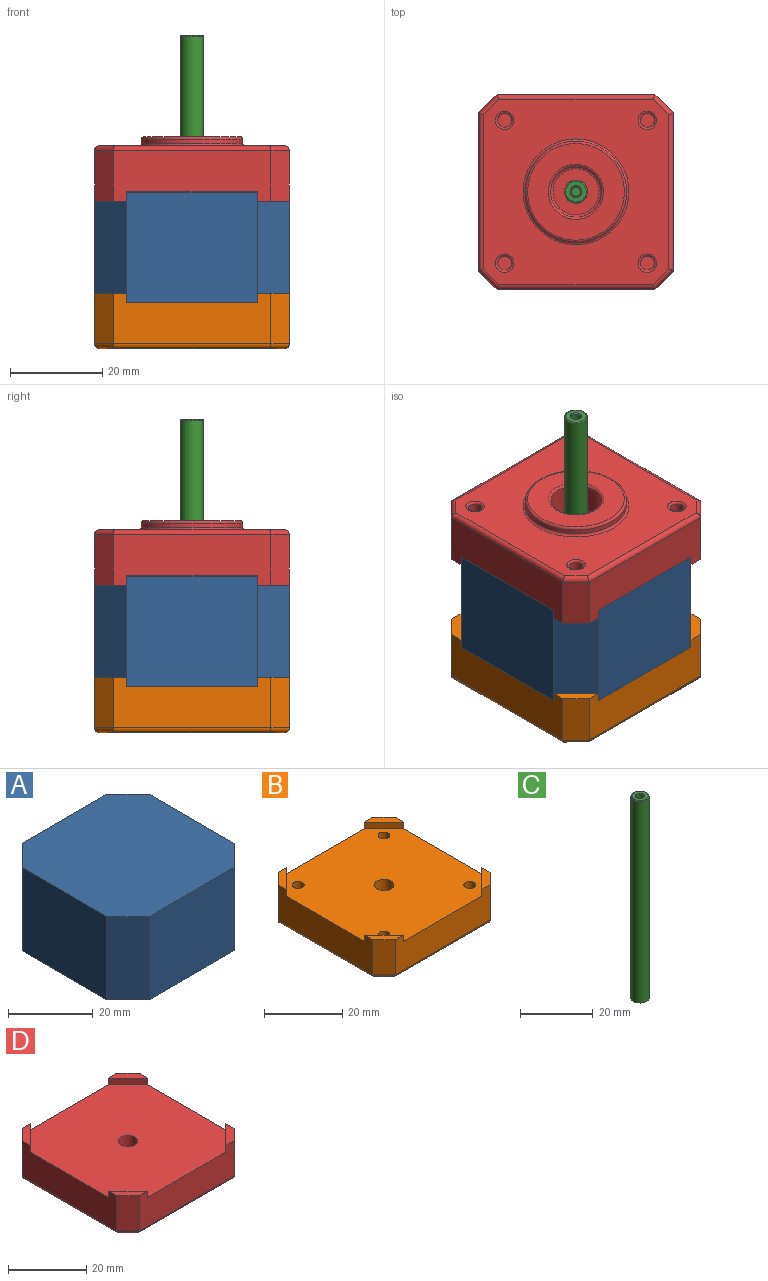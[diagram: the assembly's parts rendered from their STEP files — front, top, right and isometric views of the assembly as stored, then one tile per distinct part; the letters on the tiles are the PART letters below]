
ASSEMBLY  parts=4 mates=3
PART A: 10 faces, bbox 42.3x42.3x24 mm
  f0: plane 28.3x24mm, normal (-1,0,0), area 679.2mm2, adj f1,f7,f8,f9
  f1: plane 24x7mm, normal (-0.71,-0.71,0), area 237.6mm2, adj f0,f2,f8,f9
  f2: plane 28.3x24mm, normal (0,-1,0), area 679.2mm2, adj f1,f3,f8,f9
  f3: plane 24x7mm, normal (0.71,-0.71,0), area 237.6mm2, adj f2,f4,f8,f9
  f4: plane 28.3x24mm, normal (1,0,0), area 679.2mm2, adj f3,f5,f8,f9
  f5: plane 24x7mm, normal (0.71,0.71,0), area 237.6mm2, adj f4,f6,f8,f9
  f6: plane 28.3x24mm, normal (0,1,0), area 679.2mm2, adj f5,f7,f8,f9
  f7: plane 24x7mm, normal (-0.71,0.71,0), area 237.6mm2, adj f0,f6,f8,f9
  f8: plane 42.3x42.3mm, normal (0,0,1), area 1691.3mm2, adj f0,f1,f2,f3,f4,f5,f6,f7
  f9: plane 42.3x42.3mm, normal (0,0,-1), area 1691.3mm2, adj f0,f1,f2,f3,f4,f5,f6,f7
PART B: 50 faces, bbox 42.3x42.3x12 mm
  f0: cylinder r=2.5mm len=5mm, axis (0,0,-1), area 78.5mm2, adj f36,f37
  f1: torus R=3.6mm, axis (0,0,1), area 16.2mm2, adj f11,f31
  f2: torus R=2.6mm, axis (0,0,-1), area 14.4mm2, adj f11,f46
  f3: torus R=3.6mm, axis (0,0,1), area 16.2mm2, adj f10,f31
  f4: torus R=2.6mm, axis (0,0,-1), area 14.4mm2, adj f10,f47
  f5: torus R=3.6mm, axis (0,0,1), area 16.2mm2, adj f9,f31
  f6: torus R=2.6mm, axis (0,0,-1), area 14.4mm2, adj f9,f48
  f7: torus R=3.6mm, axis (0,0,1), area 16.2mm2, adj f8,f31
  f8: cylinder r=3.1mm len=6.2mm, axis (0,0,-1), area 48.7mm2, adj f7,f49
  f9: cylinder r=3.1mm len=6.2mm, axis (0,0,-1), area 39mm2, adj f5,f6
  f10: cylinder r=3.1mm len=6.2mm, axis (0,0,-1), area 39mm2, adj f3,f4
  f11: cylinder r=3.1mm len=6.2mm, axis (0,0,-1), area 39mm2, adj f1,f2
  f12: torus R=6.5mm, axis (0,0,1), area 57.9mm2, adj f14,f31
  f13: torus R=4.5mm, axis (0,0,-1), area 50.7mm2, adj f14,f37
  f14: cylinder r=5.5mm len=11mm, axis (0,0,-1), area 103.7mm2, adj f12,f13
  f15: cylinder r=1.5mm len=7mm, axis (0,0,-1), area 66mm2, adj f36,f46
  f16: cylinder r=1.5mm len=7mm, axis (0,0,-1), area 66mm2, adj f36,f47
  f17: cylinder r=1.5mm len=7mm, axis (0,0,-1), area 66mm2, adj f36,f48
  f18: cylinder r=1.5mm len=7mm, axis (0,0,-1), area 66mm2, adj f36,f49
  f19: plane 7x7mm, normal (0,0,1), area 16.5mm2, adj f26,f27,f28,f32
  f20: plane 7x7mm, normal (0,0,1), area 16.5mm2, adj f24,f25,f26,f33
  f21: plane 7x7mm, normal (0,0,1), area 16.5mm2, adj f22,f23,f24,f34
  f22: plane 34.3x11mm, normal (-1,0,0), area 320.7mm2, adj f21,f23,f29,f30,f34,f35,f36,f44
  f23: plane 11x4mm, normal (-0.71,-0.71,0), area 62.2mm2, adj f21,f22,f24,f42
  f24: plane 34.3x11mm, normal (0,-1,0), area 320.7mm2, adj f20,f21,f23,f25,f33,f34,f36,f40
  f25: plane 11x4mm, normal (0.71,-0.71,0), area 62.2mm2, adj f20,f24,f26,f38
  f26: plane 34.3x11mm, normal (1,0,0), area 320.7mm2, adj f19,f20,f25,f27,f32,f33,f36,f39
  f27: plane 11x4mm, normal (0.71,0.71,0), area 62.2mm2, adj f19,f26,f28,f41
  f28: plane 34.3x11mm, normal (0,1,0), area 320.7mm2, adj f19,f27,f29,f30,f32,f35,f36,f43
  f29: plane 11x4mm, normal (-0.71,0.71,0), area 62.2mm2, adj f22,f28,f30,f45
  f30: plane 7x7mm, normal (0,0,1), area 16.5mm2, adj f22,f28,f29,f35
  f31: plane 40.3x40.3mm, normal (0,0,-1), area 1305.2mm2, adj f1,f3,f5,f7,f12,f38,f39,f40
  f32: plane 7x7mm, normal (-0.71,-0.71,0), area 19.8mm2, adj f19,f26,f28,f36
  f33: plane 7x7mm, normal (-0.71,0.71,0), area 19.8mm2, adj f20,f24,f26,f36
  f34: plane 7x7mm, normal (0.71,0.71,0), area 19.8mm2, adj f21,f22,f24,f36
  f35: plane 7x7mm, normal (0.71,-0.71,0), area 19.8mm2, adj f22,f28,f30,f36
  f36: plane 42.3x42.3mm, normal (0,0,1), area 1643.4mm2, adj f0,f15,f16,f17,f18,f22,f24,f26
  f37: plane 9x9mm, normal (0,0,-1), area 44mm2, adj f0,f13
  f38: cylinder r=1mm len=4.71mm, axis (0.71,0.71,0), area 8.4mm2, adj f25,f31,f39,f40
  f39: cylinder r=1mm len=34.3mm, axis (0,1,0), area 53.4mm2, adj f26,f31,f38,f41
  f40: cylinder r=1mm len=34.3mm, axis (1,0,0), area 53.4mm2, adj f24,f31,f38,f42
  f41: cylinder r=1mm len=4.71mm, axis (-0.71,0.71,0), area 8.4mm2, adj f27,f31,f39,f43
  f42: cylinder r=1mm len=4.71mm, axis (0.71,-0.71,0), area 8.4mm2, adj f23,f31,f40,f44
  f43: cylinder r=1mm len=34.3mm, axis (-1,0,0), area 53.4mm2, adj f28,f31,f41,f45
  f44: cylinder r=1mm len=34.3mm, axis (0,-1,0), area 53.4mm2, adj f22,f31,f42,f45
  f45: cylinder r=1mm len=4.71mm, axis (-0.71,-0.71,0), area 8.4mm2, adj f29,f31,f43,f44
  f46: plane 5.2x5.2mm, normal (0,0,-1), area 14.2mm2, adj f2,f15
  f47: plane 5.2x5.2mm, normal (0,0,-1), area 14.2mm2, adj f4,f16
  f48: plane 5.2x5.2mm, normal (0,0,-1), area 14.2mm2, adj f6,f17
  f49: plane 6.2x6.2mm, normal (0,0,-1), area 23.1mm2, adj f8,f18
PART C: 7 faces, bbox 5.4x5.4x68 mm
  f0: torus R=1.25mm, axis (0,0,1), area 2.7mm2, adj f2,f4
  f1: torus R=2.25mm, axis (0,0,1), area 5.9mm2, adj f3,f4
  f2: cylinder r=1mm len=9.75mm, axis (0,0,1), area 61.3mm2, adj f0,f6
  f3: cylinder r=2.5mm len=67.75mm, axis (0,0,-1), area 1064.2mm2, adj f1,f5
  f4: plane 4.5x4.5mm, normal (0,0,1), area 11mm2, adj f0,f1
  f5: plane 5x5mm, normal (0,0,-1), area 19.6mm2, adj f3
  f6: plane 2x2mm, normal (0,0,1), area 3.1mm2, adj f2
PART D: 47 faces, bbox 42.3x42.3x14 mm
  f0: torus R=2mm, axis (0,0,-1), area 8.3mm2, adj f7,f15
  f1: torus R=2mm, axis (0,0,-1), area 8.3mm2, adj f6,f15
  f2: torus R=2mm, axis (0,0,-1), area 8.3mm2, adj f5,f15
  f3: torus R=2mm, axis (0,0,-1), area 8.3mm2, adj f4,f15
  f4: cylinder r=1.5mm len=4mm, axis (0,0,-1), area 37.7mm2, adj f3,f46
  f5: cylinder r=1.5mm len=4mm, axis (0,0,-1), area 37.7mm2, adj f2,f45
  f6: cylinder r=1.5mm len=4mm, axis (0,0,-1), area 37.7mm2, adj f1,f44
  f7: cylinder r=1.5mm len=4mm, axis (0,0,-1), area 37.7mm2, adj f0,f43
  f8: torus R=10.5mm, axis (0,0,-1), area 53.4mm2, adj f14,f33
  f9: torus R=11.5mm, axis (0,0,-1), area 55.2mm2, adj f14,f15
  f10: torus R=5mm, axis (0,0,-1), area 26.2mm2, adj f13,f34
  f11: torus R=6mm, axis (0,0,-1), area 28mm2, adj f13,f33
  f12: cylinder r=2.5mm len=5mm, axis (0,0,-1), area 78.5mm2, adj f32,f34
  f13: cylinder r=5.5mm len=11mm, axis (0,0,-1), area 207.3mm2, adj f10,f11
  f14: cylinder r=11mm len=22mm, axis (0,0,1), area 69.1mm2, adj f8,f9
  f15: plane 40.3x40.3mm, normal (0,0,-1), area 1135mm2, adj f0,f1,f2,f3,f9,f35,f36,f37
  f16: plane 7x7mm, normal (0,0,1), area 16.5mm2, adj f19,f20,f21,f28
  f17: plane 7x7mm, normal (0,0,1), area 16.5mm2, adj f19,f25,f26,f29
  f18: plane 7x7mm, normal (0,0,1), area 16.5mm2, adj f23,f24,f25,f30
  f19: plane 34.3x11mm, normal (0,1,0), area 320.7mm2, adj f16,f17,f20,f26,f28,f29,f32,f37
  f20: plane 11x4mm, normal (-0.71,0.71,0), area 62.2mm2, adj f16,f19,f21,f35
  f21: plane 34.3x11mm, normal (-1,0,0), area 320.7mm2, adj f16,f20,f22,f27,f28,f31,f32,f36
  f22: plane 11x4mm, normal (-0.71,-0.71,0), area 62.2mm2, adj f21,f23,f27,f38
  f23: plane 34.3x11mm, normal (0,-1,0), area 320.7mm2, adj f18,f22,f24,f27,f30,f31,f32,f40
  f24: plane 11x4mm, normal (0.71,-0.71,0), area 62.2mm2, adj f18,f23,f25,f42
  f25: plane 34.3x11mm, normal (1,0,0), area 320.7mm2, adj f17,f18,f24,f26,f29,f30,f32,f41
  f26: plane 11x4mm, normal (0.71,0.71,0), area 62.2mm2, adj f17,f19,f25,f39
  f27: plane 7x7mm, normal (0,0,1), area 16.5mm2, adj f21,f22,f23,f31
  f28: plane 7x7mm, normal (0.71,-0.71,0), area 19.8mm2, adj f16,f19,f21,f32
  f29: plane 7x7mm, normal (-0.71,-0.71,0), area 19.8mm2, adj f17,f19,f25,f32
  f30: plane 7x7mm, normal (-0.71,0.71,0), area 19.8mm2, adj f18,f23,f25,f32
  f31: plane 7x7mm, normal (0.71,0.71,0), area 19.8mm2, adj f21,f23,f27,f32
  f32: plane 42.3x42.3mm, normal (0,0,1), area 1671.7mm2, adj f12,f19,f21,f23,f25,f28,f29,f30
  f33: plane 21x21mm, normal (0,0,-1), area 233.3mm2, adj f8,f11
  f34: plane 10x10mm, normal (0,0,-1), area 58.9mm2, adj f10,f12
  f35: cylinder r=1mm len=4.71mm, axis (0.71,0.71,0), area 8.4mm2, adj f15,f20,f36,f37
  f36: cylinder r=1mm len=34.3mm, axis (0,1,0), area 53.4mm2, adj f15,f21,f35,f38
  f37: cylinder r=1mm len=34.3mm, axis (1,0,0), area 53.4mm2, adj f15,f19,f35,f39
  f38: cylinder r=1mm len=4.71mm, axis (-0.71,0.71,0), area 8.4mm2, adj f15,f22,f36,f40
  f39: cylinder r=1mm len=4.71mm, axis (0.71,-0.71,0), area 8.4mm2, adj f15,f26,f37,f41
  f40: cylinder r=1mm len=34.3mm, axis (-1,0,0), area 53.4mm2, adj f15,f23,f38,f42
  f41: cylinder r=1mm len=34.3mm, axis (0,-1,0), area 53.4mm2, adj f15,f25,f39,f42
  f42: cylinder r=1mm len=4.71mm, axis (-0.71,-0.71,0), area 8.4mm2, adj f15,f24,f40,f41
  f43: plane 3x3mm, normal (0,0,-1), area 7.1mm2, adj f7
  f44: plane 3x3mm, normal (0,0,-1), area 7.1mm2, adj f6
  f45: plane 3x3mm, normal (0,0,-1), area 7.1mm2, adj f5
  f46: plane 3x3mm, normal (0,0,-1), area 7.1mm2, adj f4
PLACE A t=(-7.93,34.71,-29.44)mm
PLACE B rot(axis=(0,0,1),0deg) t=(-7.93,34.71,-39.44)mm fixed
PLACE C rot(axis=(0,0,-1),96.9deg) t=(-7.93,34.71,-39.44)mm
PLACE D rot(axis=(0,1,0),180deg) t=(-7.93,34.71,4.56)mm
MATE fastened B.f0 <-> A.f9  axis (0,0,1) through (-7.93,34.71,-29.44)mm
MATE revolute B.f0 <-> C.f0  axis (0,0,-1) through (-7.93,34.71,-39.44)mm
MATE fastened A.f8 <-> D.f8  axis (0,0,1) through (-7.93,34.71,-5.44)mm
